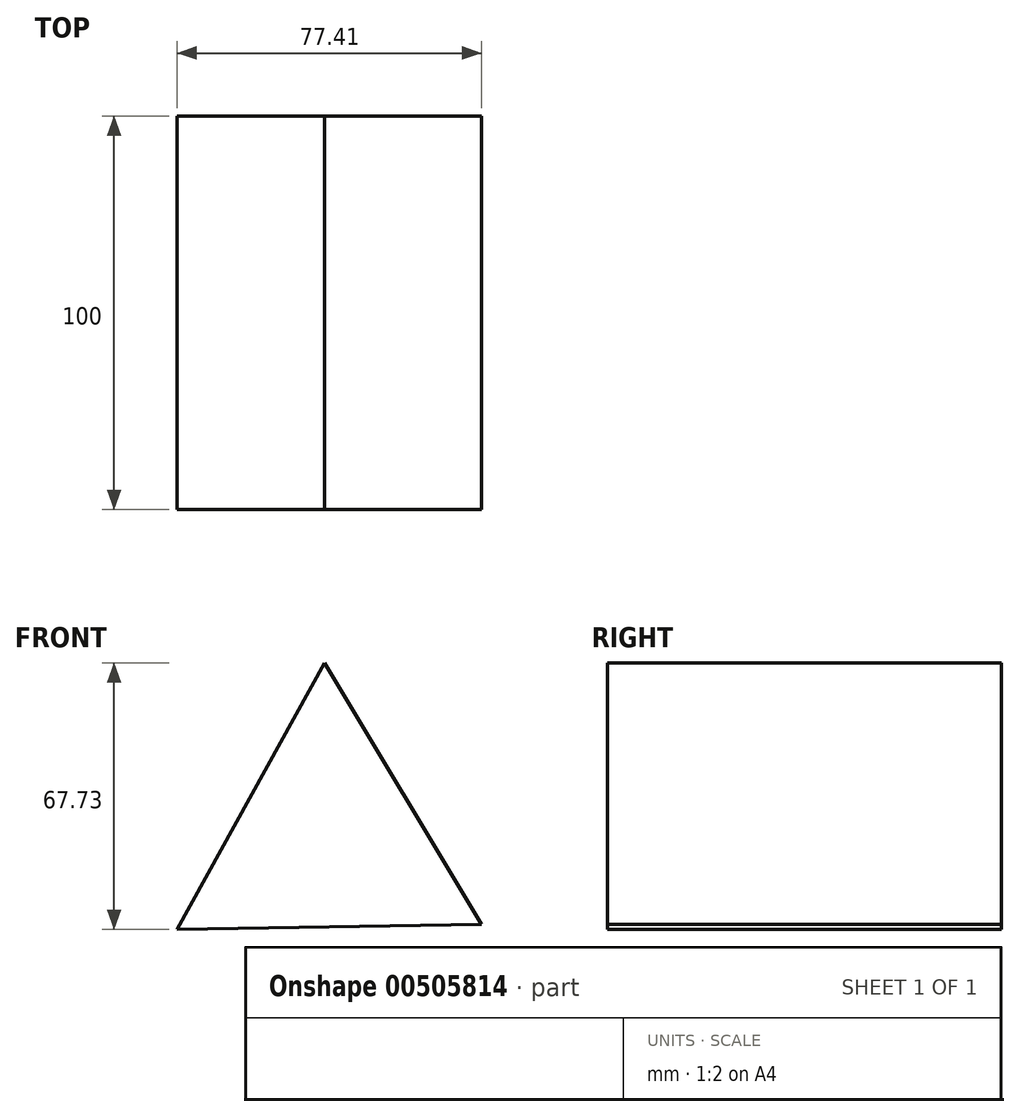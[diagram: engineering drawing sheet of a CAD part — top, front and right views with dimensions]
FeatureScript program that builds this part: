
annotation { "Feature Type Name" : "Feature", "Feature Type Description" : "" }
export const myFeature = defineFeature(function(context is Context, id is Id, definition is map)
    precondition{}
    {
        {
            var Q0;
            Q0=qCreatedBy(makeId("Front.planeOp"),FACE);
            var sketch = newSketch(context, id + "F0", { "sketchPlane" : qUnion([Q0])});
            skCircle(sketch, "E0.cCircle", {"center": v(0, 0) * mm, "radius": 22.35 * mm, "construction": true});
            skLineSegment(sketch, "E0.0", {"start": v(-38.3, -23.04) * mm, "end": v(-0.8, 44.7) * mm});
            skLineSegment(sketch, "E0.1", {"start": v(-0.8, 44.7) * mm, "end": v(39.1, -21.66) * mm});
            skLineSegment(sketch, "E0.2", {"start": v(39.1, -21.66) * mm, "end": v(-38.3, -23.04) * mm});
            skPoint(sketch, "E0.0.midPoint", {"position": v(-19.55, 10.83) * mm});
            skSolve(sketch);
        }
        {
            var Q0;
            Q0 = qSketchRegion(id + "F0", true);
            extrude(context, id + "F1", {"entities" : qUnion([Q0]), "endBound" : BoundingType.SYMMETRIC, "depth" : 100 * mm});
        }
    });
